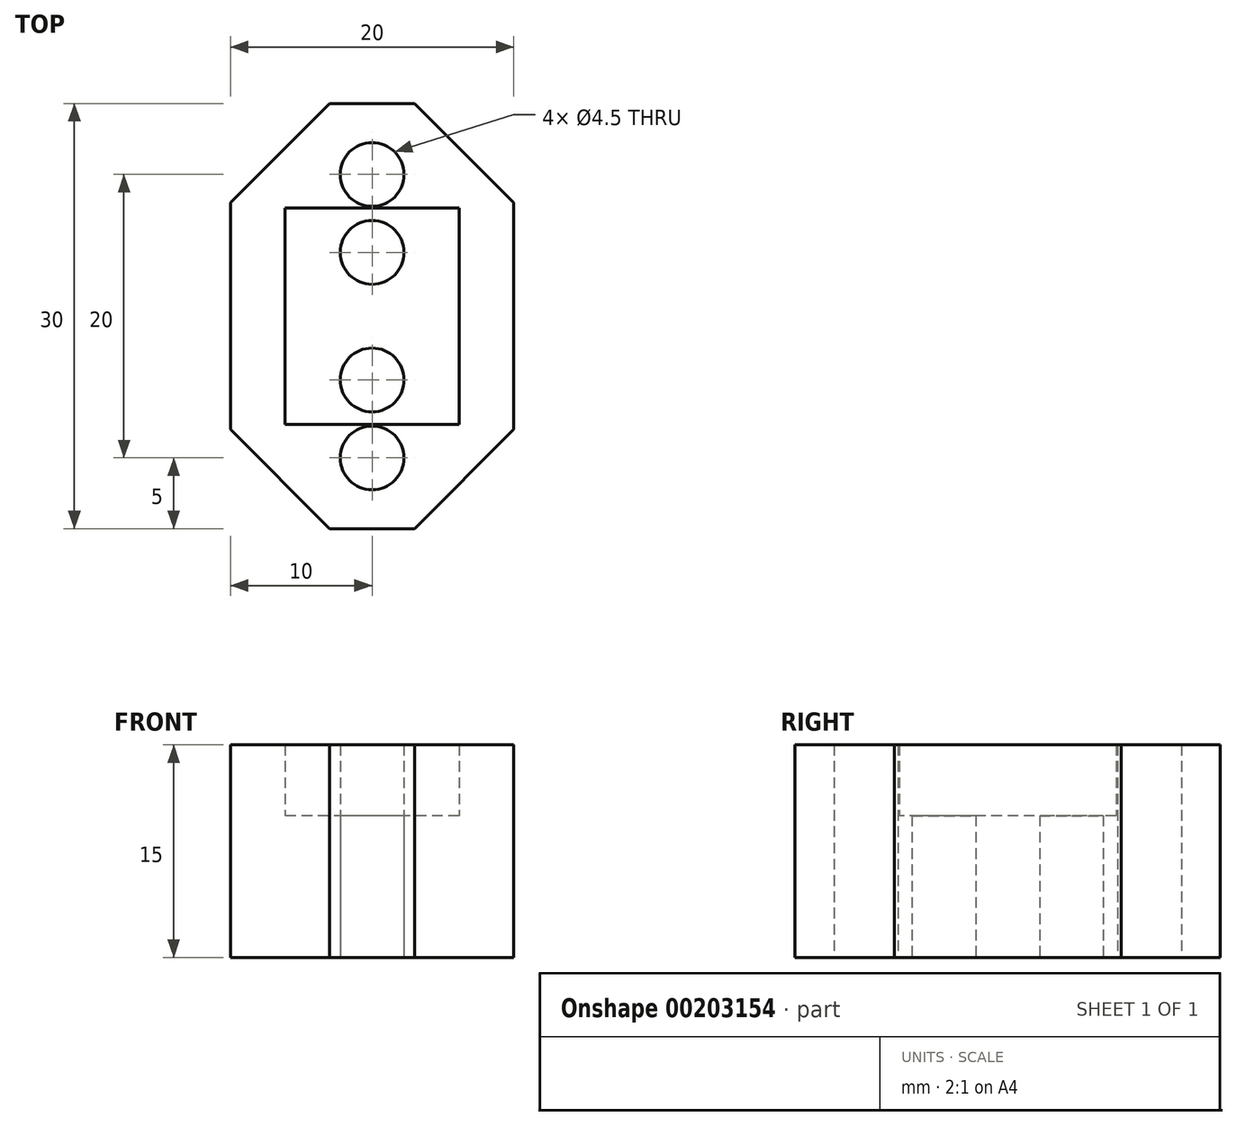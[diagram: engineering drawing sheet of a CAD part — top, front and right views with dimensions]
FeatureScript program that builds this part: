
annotation { "Feature Type Name" : "Feature", "Feature Type Description" : "" }
export const myFeature = defineFeature(function(context is Context, id is Id, definition is map)
    precondition{}
    {
        {
            var Q0;
            Q0=qCreatedBy(makeId("Top.planeOp"),FACE);
            var sketch = newSketch(context, id + "F0", { "sketchPlane" : qUnion([Q0])});
            skLineSegment(sketch, "E0.bottom", {"start": v(10, 15) * mm, "end": v(-10, 15) * mm});
            skLineSegment(sketch, "E0.top", {"start": v(10, -15) * mm, "end": v(-10, -15) * mm});
            skLineSegment(sketch, "E0.left", {"start": v(10, 15) * mm, "end": v(10, -15) * mm});
            skLineSegment(sketch, "E0.right", {"start": v(-10, 15) * mm, "end": v(-10, -15) * mm});
            skPoint(sketch, "E0.middle", {"position": v(0, 0) * mm});
            skLineSegment(sketch, "E1", {"start": v(0, 0) * mm, "end": v(0, 10) * mm});
            skLineSegment(sketch, "E2", {"start": v(0, 0) * mm, "end": v(0, -10) * mm});
            skCircle(sketch, "E3", {"center": v(0, 10) * mm, "radius": 2.25 * mm});
            skCircle(sketch, "E4", {"center": v(0, -10) * mm, "radius": 2.25 * mm});
            skLineSegment(sketch, "E5", {"start": v(0, 0) * mm, "end": v(0, 4.5) * mm});
            skLineSegment(sketch, "E6", {"start": v(0, 0) * mm, "end": v(0, -4.5) * mm});
            skCircle(sketch, "E7", {"center": v(0, -4.5) * mm, "radius": 2.25 * mm});
            skCircle(sketch, "E8", {"center": v(0, 4.5) * mm, "radius": 2.25 * mm});
            skSolve(sketch);
        }
        {
            var Q0;
            Q0=makeQuery(id+"F0.imprint","IMPRINT",FACE,{"disambiguationData":[TD([[makeQuery(id+"F0.imprint","IMPRINT",EDGE,{"derivedFrom":sQuery(id+"F0.wireOp",EDGE,"E0.bottom")}),1.0]])]});
            extrude(context, id + "F1", {"entities" : qUnion([Q0]), "depth" : 10 * mm});
        }
        {
            var Q0;
            Q0=makeQuery(id+"F1.opExtrude","CAP_FACE",FACE,{"disambiguationData":[OSD([sQuery(id+"F0.wireOp",EDGE,"E0.bottom"),sQuery(id+"F0.wireOp",EDGE,"E0.top"),sQuery(id+"F0.wireOp",EDGE,"E0.left"),sQuery(id+"F0.wireOp",EDGE,"E0.right"),sQuery(id+"F0.wireOp",EDGE,"E3"),sQuery(id+"F0.wireOp",EDGE,"E4"),sQuery(id+"F0.wireOp",EDGE,"E7"),sQuery(id+"F0.wireOp",EDGE,"E8")])],"isStart":false});
            var sketch = newSketch(context, id + "F2", { "sketchPlane" : qUnion([Q0])});
            skLineSegment(sketch, "E9.bottom", {"start": v(-10, 15) * mm, "end": v(10, 15) * mm});
            skLineSegment(sketch, "E9.top", {"start": v(-10, -15) * mm, "end": v(10, -15) * mm});
            skLineSegment(sketch, "E9.left", {"start": v(-10, 15) * mm, "end": v(-10, -15) * mm});
            skLineSegment(sketch, "E9.right", {"start": v(10, 15) * mm, "end": v(10, -15) * mm});
            skLineSegment(sketch, "E10.bottom", {"start": v(6.13, 7.64) * mm, "end": v(-6.13, 7.64) * mm});
            skLineSegment(sketch, "E10.top", {"start": v(6.13, -7.64) * mm, "end": v(-6.13, -7.64) * mm});
            skLineSegment(sketch, "E10.left", {"start": v(6.13, 7.64) * mm, "end": v(6.13, -7.64) * mm});
            skLineSegment(sketch, "E10.right", {"start": v(-6.13, 7.64) * mm, "end": v(-6.13, -7.64) * mm});
            skPoint(sketch, "E10.middle", {"position": v(0, 0) * mm});
            skLineSegment(sketch, "E11", {"start": v(0, 0) * mm, "end": v(0, 10) * mm});
            skLineSegment(sketch, "E12", {"start": v(0, 10) * mm, "end": v(0, -10) * mm});
            skCircle(sketch, "E13", {"center": v(0, -10) * mm, "radius": 2.25 * mm});
            skCircle(sketch, "E14", {"center": v(0, 10) * mm, "radius": 2.25 * mm});
            skSolve(sketch);
        }
        {
            var Q0;
            Q0 = qSketchRegion(id + "F2", true);
            extrude(context, id + "F3", {"entities" : qUnion([Q0]), "operationType" : NewBodyOperationType.ADD, "depth" : 5 * mm});
        }
        {
            var Q0;
            Q0=makeQuery(id+"F3.boolean.opBoolean","MERGE",EDGE,{"derivedFrom":[makeQuery(id+"F1.opExtrude","SWEPT_EDGE",EDGE,{"disambiguationData":[OSD([sQuery(id+"F0.wireOp",EDGE,"E0.bottom"),sQuery(id+"F0.wireOp",EDGE,"E0.right")])]}),makeQuery(id+"F3.opExtrude","SWEPT_EDGE",EDGE,{"disambiguationData":[OSD([sQuery(id+"F2.wireOp",EDGE,"E9.bottom"),sQuery(id+"F2.wireOp",EDGE,"E9.left")])]})]});
            var Q1;
            Q1=makeQuery(id+"F3.boolean.opBoolean","MERGE",EDGE,{"derivedFrom":[makeQuery(id+"F1.opExtrude","SWEPT_EDGE",EDGE,{"disambiguationData":[OSD([sQuery(id+"F0.wireOp",EDGE,"E0.top"),sQuery(id+"F0.wireOp",EDGE,"E0.right")])]}),makeQuery(id+"F3.opExtrude","SWEPT_EDGE",EDGE,{"disambiguationData":[OSD([sQuery(id+"F2.wireOp",EDGE,"E9.top"),sQuery(id+"F2.wireOp",EDGE,"E9.left")])]})]});
            var Q2;
            Q2=makeQuery(id+"F3.boolean.opBoolean","MERGE",EDGE,{"derivedFrom":[makeQuery(id+"F1.opExtrude","SWEPT_EDGE",EDGE,{"disambiguationData":[OSD([sQuery(id+"F0.wireOp",EDGE,"E0.bottom"),sQuery(id+"F0.wireOp",EDGE,"E0.left")])]}),makeQuery(id+"F3.opExtrude","SWEPT_EDGE",EDGE,{"disambiguationData":[OSD([sQuery(id+"F2.wireOp",EDGE,"E9.bottom"),sQuery(id+"F2.wireOp",EDGE,"E9.right")])]})]});
            var Q3;
            Q3=makeQuery(id+"F3.boolean.opBoolean","MERGE",EDGE,{"derivedFrom":[makeQuery(id+"F1.opExtrude","SWEPT_EDGE",EDGE,{"disambiguationData":[OSD([sQuery(id+"F0.wireOp",EDGE,"E0.top"),sQuery(id+"F0.wireOp",EDGE,"E0.left")])]}),makeQuery(id+"F3.opExtrude","SWEPT_EDGE",EDGE,{"disambiguationData":[OSD([sQuery(id+"F2.wireOp",EDGE,"E9.top"),sQuery(id+"F2.wireOp",EDGE,"E9.right")])]})]});
            chamfer(context, id + "F4", {"entities" : qUnion([Q0, Q1, Q2, Q3]), "width" : 7 * mm, "tangentPropagation" : true});
        }
    });
